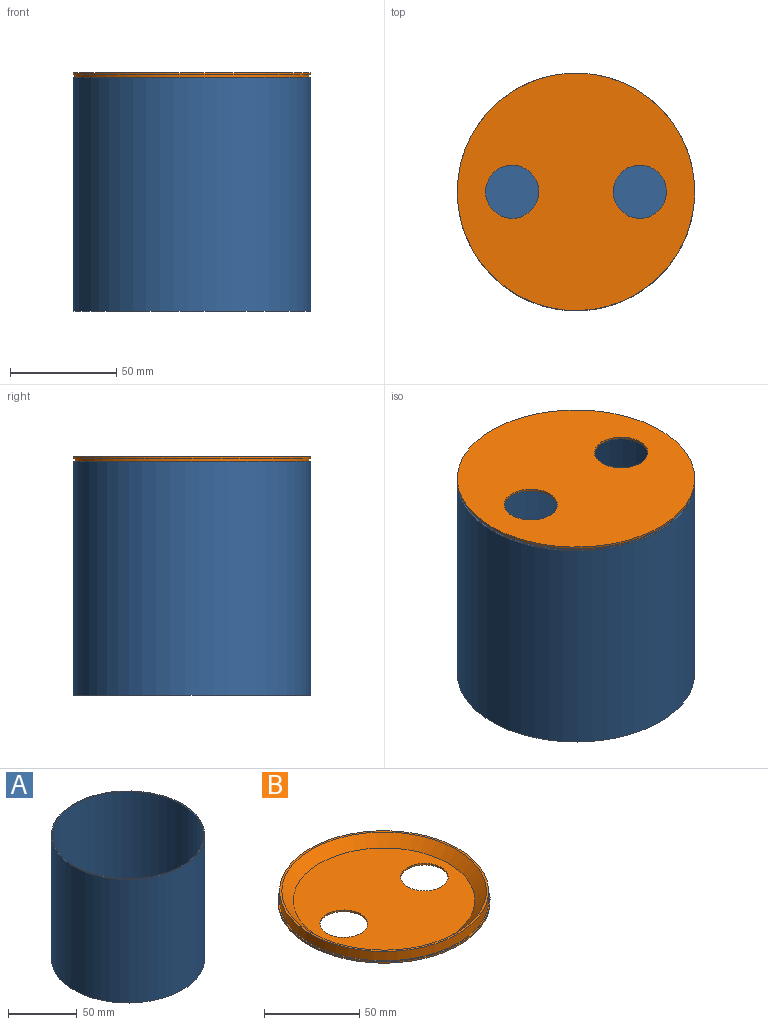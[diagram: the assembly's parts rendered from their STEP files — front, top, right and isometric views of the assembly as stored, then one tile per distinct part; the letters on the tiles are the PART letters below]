
ASSEMBLY  parts=2 mates=1
PART A: 6 faces, bbox 111.6x111.6x110 mm
  f0: cylinder r=55mm len=110mm, axis (0,0,-1), area 35732.5mm2, adj f2,f5
  f1: cylinder r=55.8mm len=111.6mm, axis (0,0,-1), area 38566.2mm2, adj f2,f3
  f2: plane 111.6x111.6mm, normal (0,0,1), area 278.5mm2, adj f0,f1
  f3: plane 111.6x111.6mm, normal (0,0,-1), area 9781.8mm2, adj f1
  f4: plane 98x98mm, normal (0,0,1), area 7543mm2, adj f5
  f5: cone r=49mm half-angle=45deg, axis (0,0,1), area 2772.4mm2, adj f0,f4
PART B: 9 faces, bbox 111.6x111.6x7 mm
  f0: cylinder r=55mm len=110mm, axis (0,0,-1), area 2073.5mm2, adj f1,f7
  f1: plane 110x110mm, normal (0,0,1), area 410.2mm2, adj f0,f8
  f2: plane 95.6x95.6mm, normal (0,0,1), area 6196.3mm2, adj f3,f4,f8
  f3: cylinder r=12.5mm len=25mm, axis (0,0,1), area 78.5mm2, adj f2,f6
  f4: cylinder r=12.5mm len=25mm, axis (0,0,1), area 78.5mm2, adj f2,f6
  f5: cylinder r=55.8mm len=111.6mm, axis (0,0,1), area 350.6mm2, adj f6,f7
  f6: plane 111.6x111.6mm, normal (0,0,-1), area 8800mm2, adj f3,f4,f5
  f7: plane 111.6x111.6mm, normal (0,0,1), area 278.5mm2, adj f0,f5
  f8: cone r=47.8mm half-angle=45deg, axis (0,0,1), area 2708.4mm2, adj f1,f2
PLACE A at identity fixed
PLACE B rot(axis=(0,1,0),180deg) t=(0,0,111.17)mm
MATE slider B.f0 <-> A.f0  axis (0,0,1) through (0,0,108.17)mm
